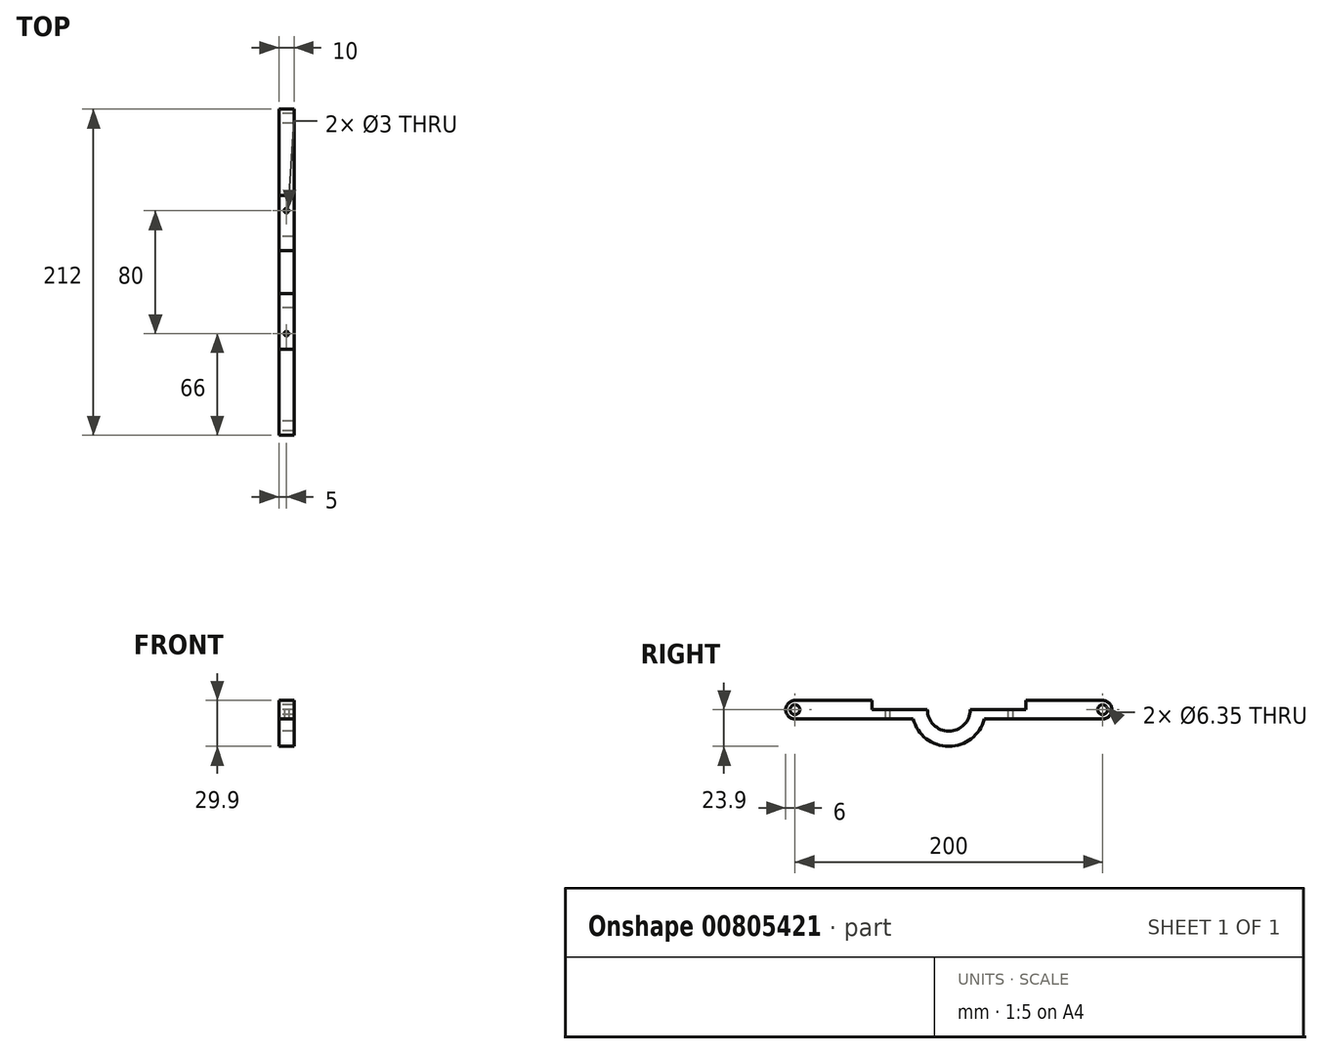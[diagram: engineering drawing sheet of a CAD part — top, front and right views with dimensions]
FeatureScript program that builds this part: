
annotation { "Feature Type Name" : "Feature", "Feature Type Description" : "" }
export const myFeature = defineFeature(function(context is Context, id is Id, definition is map)
    precondition{}
    {
        {
            var Q0;
            Q0=qCreatedBy(makeId("Right.planeOp"),FACE);
            var sketch = newSketch(context, id + "F0", { "sketchPlane" : qUnion([Q0])});
            skArc(sketch, "E0", {"start": v(0, -13.9) * mm, "mid": v(-9.83, -9.83) * mm, "end": v(-13.9, 0) * mm});
            skArc(sketch, "E1", {"start": v(0, -23.9) * mm, "mid": v(-14.63, -18.9) * mm, "end": v(-23.13, -6) * mm});
            skLineSegment(sketch, "E2.bottom", {"start": v(-100, 6) * mm, "end": v(-50, 6) * mm});
            skLineSegment(sketch, "E2.top", {"start": v(-100, -6) * mm, "end": v(-23.13, -6) * mm});
            skPoint(sketch, "E2.right.end.orphan", {"position": v(100, -6) * mm});
            skPoint(sketch, "E2.right.start.orphan", {"position": v(100, 6) * mm});
            skLineSegment(sketch, "E3.top", {"start": v(-50, 0) * mm, "end": v(-13.9, 0) * mm});
            skLineSegment(sketch, "E3.left", {"start": v(-50, 6) * mm, "end": v(-50, 0) * mm});
            skPoint(sketch, "E4.orphan", {"position": v(-23.9, 0) * mm});
            skPoint(sketch, "E5", {"position": v(-100, 0) * mm});
            skArc(sketch, "E6", {"start": v(-100, -6) * mm, "mid": v(-106, 0) * mm, "end": v(-100, 6) * mm});
            skCircle(sketch, "E7", {"center": v(-100, 0) * mm, "radius": 3.17 * mm});
            skCircle(sketch, "E8.MirrorC", {"center": v(100, 0) * mm, "radius": 3.17 * mm});
            skLineSegment(sketch, "E9.MirrorCS", {"start": v(50, 0) * mm, "end": v(13.9, 0) * mm});
            skPoint(sketch, "E10.MirrorP", {"position": v(23.9, 0) * mm});
            skLineSegment(sketch, "E11.MirrorCS", {"start": v(50, 6) * mm, "end": v(50, 0) * mm});
            skArc(sketch, "E12.MirrorCS", {"start": v(0, -13.9) * mm, "mid": v(9.83, -9.83) * mm, "end": v(13.9, 0) * mm});
            skLineSegment(sketch, "E13.MirrorCS", {"start": v(100, 6) * mm, "end": v(50, 6) * mm});
            skArc(sketch, "E14.MirrorCS", {"start": v(0, -23.9) * mm, "mid": v(14.63, -18.9) * mm, "end": v(23.13, -6) * mm});
            skLineSegment(sketch, "E15.MirrorCS", {"start": v(100, -6) * mm, "end": v(23.13, -6) * mm});
            skArc(sketch, "E16.MirrorCS", {"start": v(100, -6) * mm, "mid": v(106, 0) * mm, "end": v(100, 6) * mm});
            skLineSegment(sketch, "E17.MirrorCS", {"start": v(0, -13.9) * mm, "end": v(0, -23.9) * mm});
            skSolve(sketch);
        }
        {
            var Q0;
            Q0 = qSketchRegion(id + "F0", true);
            extrude(context, id + "F1", {"entities" : qUnion([Q0]), "depth" : 10 * mm, "offsetDistance" : 25 * mm});
        }
        {
            var Q0;
            Q0=makeQuery(id+"F1.opExtrude","SWEPT_FACE",FACE,{"disambiguationData":[OSD([sQuery(id+"F0.wireOp",EDGE,"E2.top")])]});
            var sketch = newSketch(context, id + "F2", { "sketchPlane" : qUnion([Q0])});
            skPoint(sketch, "E18.0", {"position": v(5, 100) * mm});
            skPoint(sketch, "E19.0", {"position": v(5, -100) * mm});
            skLineSegment(sketch, "E20", {"start": v(5, 100) * mm, "end": v(5, -100) * mm, "construction": true});
            skCircle(sketch, "E21", {"center": v(5, 40) * mm, "radius": 1.5 * mm});
            skCircle(sketch, "E22.MirrorC", {"center": v(5, -40) * mm, "radius": 1.5 * mm});
            skSolve(sketch);
        }
        {
            var Q0;
            Q0 = qSketchRegion(id + "F2", true);
            extrude(context, id + "F3", {"entities" : qUnion([Q0]), "operationType" : NewBodyOperationType.REMOVE, "oppositeDirection" : true, "depth" : 25 * mm, "offsetDistance" : 25 * mm});
        }
    });
